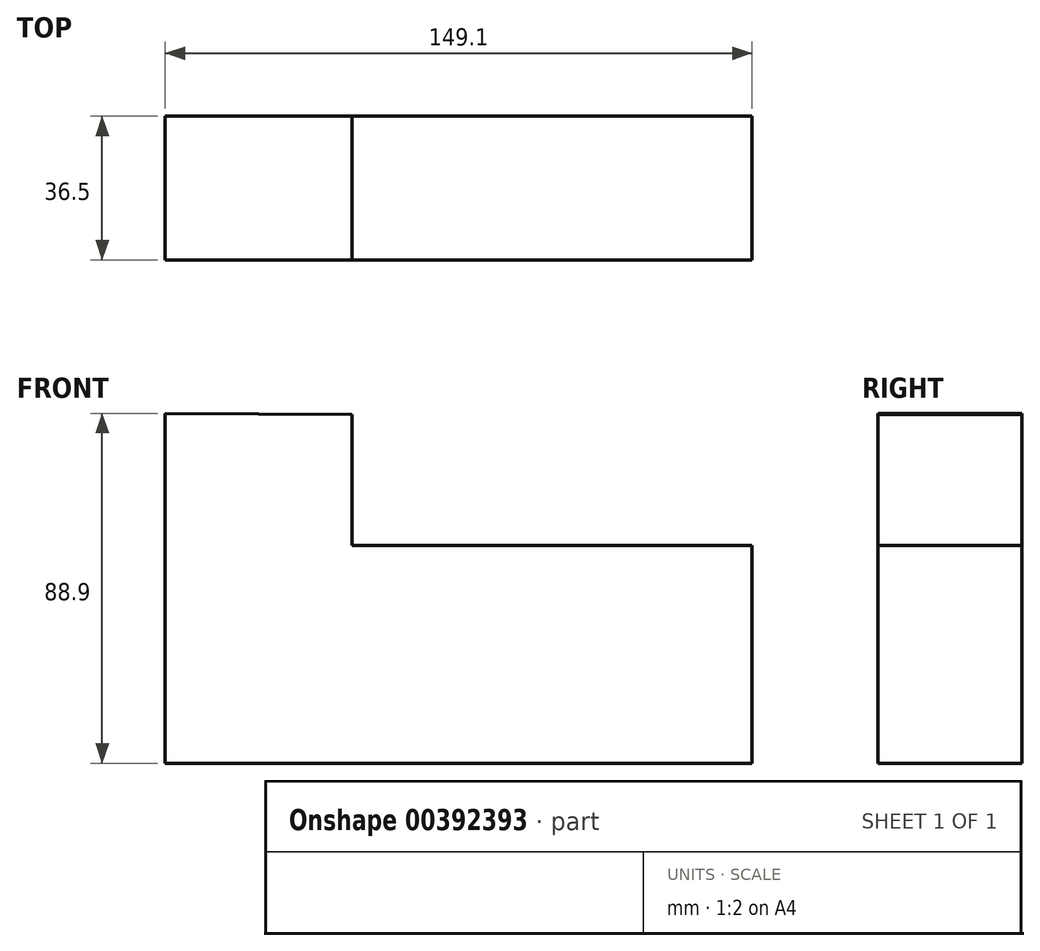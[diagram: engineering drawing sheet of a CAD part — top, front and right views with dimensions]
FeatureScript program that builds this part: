
annotation { "Feature Type Name" : "Feature", "Feature Type Description" : "" }
export const myFeature = defineFeature(function(context is Context, id is Id, definition is map)
    precondition{}
    {
        {
            var Q0;
            Q0=qCreatedBy(makeId("Front.planeOp"),FACE);
            var sketch = newSketch(context, id + "F0", { "sketchPlane" : qUnion([Q0])});
            skLineSegment(sketch, "E0", {"start": v(-65.42, 38.74) * mm, "end": v(-65.42, -50.16) * mm});
            skLineSegment(sketch, "E1", {"start": v(-65.42, -50.16) * mm, "end": v(83.68, -50.16) * mm});
            skLineSegment(sketch, "E2", {"start": v(83.68, -50.16) * mm, "end": v(83.68, 5.21) * mm});
            skLineSegment(sketch, "E3", {"start": v(83.68, 5.21) * mm, "end": v(-17.92, 5.21) * mm});
            skLineSegment(sketch, "E4", {"start": v(-17.92, 5.21) * mm, "end": v(-17.92, 38.49) * mm});
            skLineSegment(sketch, "E5", {"start": v(-65.42, 38.74) * mm, "end": v(-17.92, 38.49) * mm});
            skSolve(sketch);
        }
        {
            var Q0;
            Q0=makeQuery(id+"F0.imprint","IMPRINT",FACE,{"disambiguationData":[TD([[makeQuery(id+"F0.imprint","IMPRINT",EDGE,{"derivedFrom":sQuery(id+"F0.wireOp",EDGE,"E0")}),1.0]])]});
            extrude(context, id + "F1", {"entities" : qUnion([Q0]), "depth" : 36.5 * mm});
        }
    });
